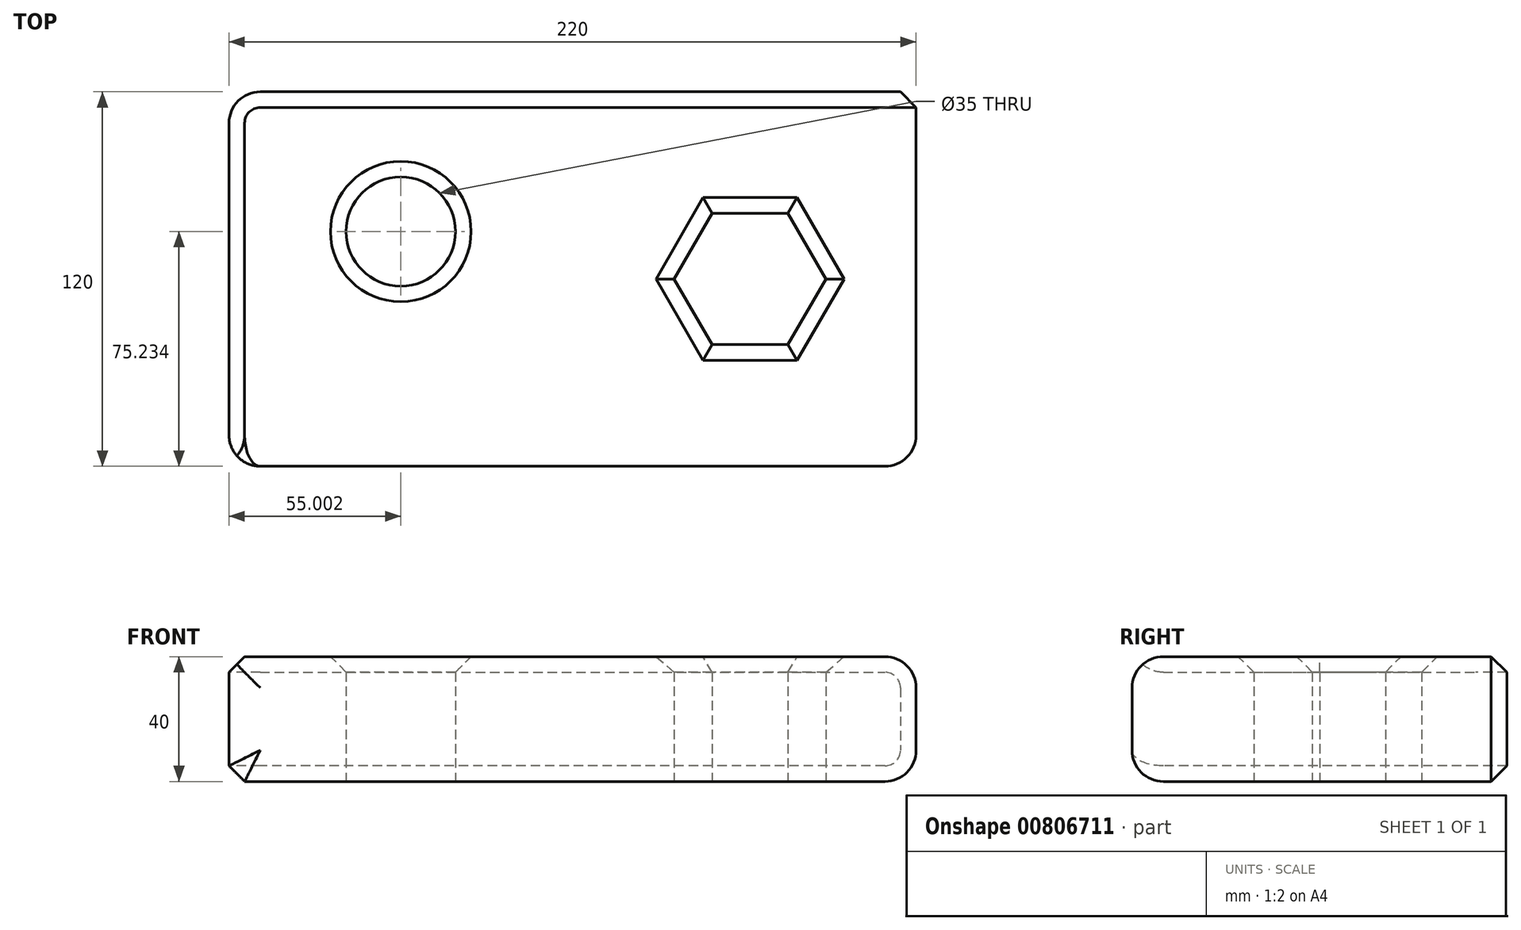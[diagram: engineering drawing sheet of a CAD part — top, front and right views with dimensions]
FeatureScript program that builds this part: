
annotation { "Feature Type Name" : "Feature", "Feature Type Description" : "" }
export const myFeature = defineFeature(function(context is Context, id is Id, definition is map)
    precondition{}
    {
        {
            var Q0;
            Q0=qCreatedBy(makeId("Top.planeOp"),FACE);
            var sketch = newSketch(context, id + "F0", { "sketchPlane" : qUnion([Q0])});
            skLineSegment(sketch, "E0.bottom", {"start": v(-98.83, 59.95) * mm, "end": v(111.17, 59.95) * mm});
            skLineSegment(sketch, "E0.top", {"start": v(-108.83, -60.05) * mm, "end": v(101.17, -60.05) * mm});
            skLineSegment(sketch, "E0.left", {"start": v(-108.83, 49.95) * mm, "end": v(-108.83, -60.05) * mm});
            skLineSegment(sketch, "E0.right", {"start": v(111.17, 59.95) * mm, "end": v(111.17, -50.05) * mm});
            skPoint(sketch, "E1.visualSharp", {"position": v(-108.83, 59.95) * mm});
            skArc(sketch, "E1.filletArc", {"start": v(-98.83, 59.95) * mm, "mid": v(-105.9, 57.02) * mm, "end": v(-108.83, 49.95) * mm});
            skPoint(sketch, "E2.visualSharp", {"position": v(111.17, -60.05) * mm});
            skArc(sketch, "E2.filletArc", {"start": v(101.17, -60.05) * mm, "mid": v(108.24, -57.12) * mm, "end": v(111.17, -50.05) * mm});
            skCircle(sketch, "E3", {"center": v(-53.83, 15.18) * mm, "radius": 17.5 * mm});
            skCircle(sketch, "E4.cCircle", {"center": v(58.02, 0) * mm, "radius": 21.06 * mm, "construction": true});
            skLineSegment(sketch, "E4.0", {"start": v(45.86, 21.06) * mm, "end": v(70.18, 21.06) * mm});
            skLineSegment(sketch, "E4.1", {"start": v(70.18, 21.06) * mm, "end": v(82.34, 0) * mm});
            skLineSegment(sketch, "E4.2", {"start": v(82.34, 0) * mm, "end": v(70.18, -21.06) * mm});
            skLineSegment(sketch, "E4.3", {"start": v(70.18, -21.06) * mm, "end": v(45.86, -21.06) * mm});
            skLineSegment(sketch, "E4.4", {"start": v(45.86, -21.06) * mm, "end": v(33.7, 0) * mm});
            skLineSegment(sketch, "E4.5", {"start": v(33.7, 0) * mm, "end": v(45.86, 21.06) * mm});
            skPoint(sketch, "E4.0.midPoint", {"position": v(58.02, 21.06) * mm});
            skSolve(sketch);
        }
        {
            var Q0;
            Q0=makeQuery(id+"F0.imprint","IMPRINT",FACE,{"disambiguationData":[TD([[makeQuery(id+"F0.imprint","IMPRINT",EDGE,{"derivedFrom":sQuery(id+"F0.wireOp",EDGE,"E0.bottom")}),-1.0]])]});
            extrude(context, id + "F1", {"entities" : qUnion([Q0]), "depth" : 40 * mm, "offsetDistance" : 25 * mm});
        }
        {
            var Q0;
            Q0=makeQuery(id+"F1.opExtrude","SWEPT_FACE",FACE,{"disambiguationData":[OSD([sQuery(id+"F0.wireOp",EDGE,"E0.top")])]});
            fillet(context, id + "F2", {"entities" : qUnion([Q0]), "radius" : 10 * mm, "tangentPropagation" : true, "allowEdgeOverflow" : false});
        }
        {
            var Q0;
            Q0=makeQuery(id+"F1.opExtrude","CAP_FACE",FACE,{"disambiguationData":[OSD([sQuery(id+"F0.wireOp",EDGE,"E0.bottom"),sQuery(id+"F0.wireOp",EDGE,"E0.top"),sQuery(id+"F0.wireOp",EDGE,"E0.left"),sQuery(id+"F0.wireOp",EDGE,"E0.right"),sQuery(id+"F0.wireOp",EDGE,"E1.filletArc"),sQuery(id+"F0.wireOp",EDGE,"E2.filletArc"),sQuery(id+"F0.wireOp",EDGE,"E3"),sQuery(id+"F0.wireOp",EDGE,"E4.0"),sQuery(id+"F0.wireOp",EDGE,"E4.1"),sQuery(id+"F0.wireOp",EDGE,"E4.2"),sQuery(id+"F0.wireOp",EDGE,"E4.3"),sQuery(id+"F0.wireOp",EDGE,"E4.4"),sQuery(id+"F0.wireOp",EDGE,"E4.5")])],"isStart":false});
            chamfer(context, id + "F3", {"entities" : qUnion([Q0]), "width" : 5 * mm, "tangentPropagation" : true});
        }
    });
